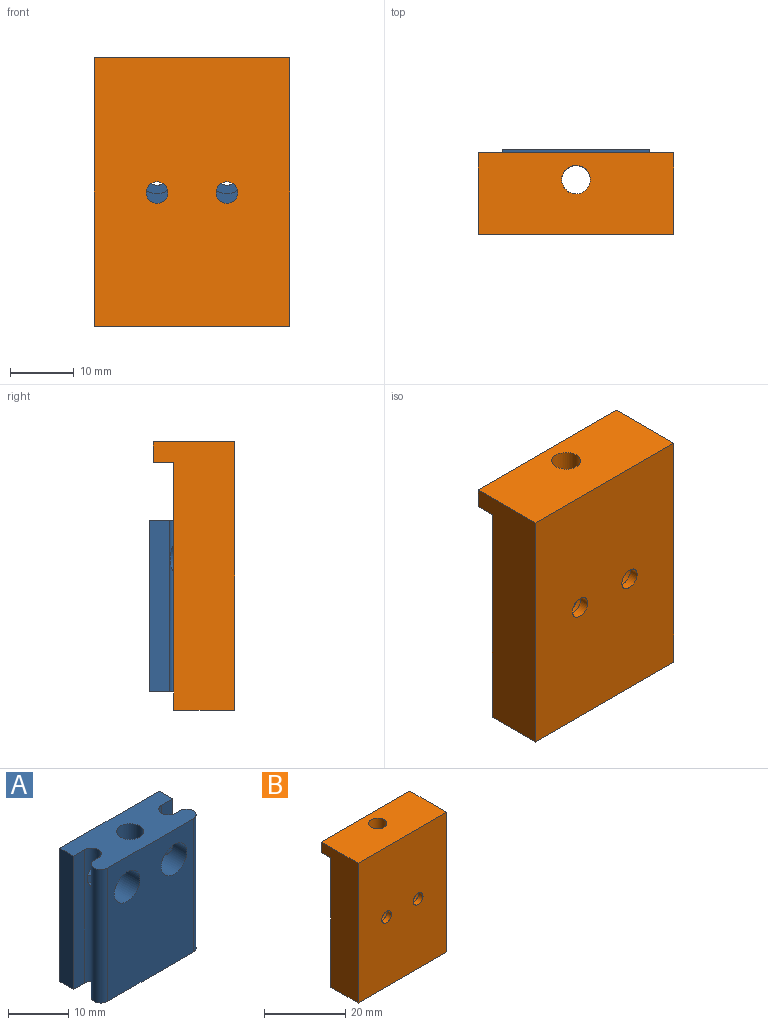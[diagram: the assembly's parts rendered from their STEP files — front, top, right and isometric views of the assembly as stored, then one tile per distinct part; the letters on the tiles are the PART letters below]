
ASSEMBLY  parts=2 mates=1
PART A: 28 faces, bbox 23.2x9.6x27 mm
  f0: plane 23.22x9.6mm, normal (0,0,-1), area 147.3mm2, adj f1,f2,f3,f4,f5,f6,f7,f8
  f1: cylinder r=1.6mm len=27mm, axis (0,0,-1), area 120.8mm2, adj f0,f3,f4,f13,f17
  f2: cylinder r=1.6mm len=27mm, axis (0,0,-1), area 120.8mm2, adj f0,f8,f9,f13,f16
  f3: plane 27x1mm, normal (0,1,0), area 27mm2, adj f0,f1,f12,f13
  f4: plane 27x2.6mm, normal (0,-1,0), area 70.2mm2, adj f0,f1,f5,f13
  f5: plane 27x3.2mm, normal (1,0,0), area 86.4mm2, adj f0,f4,f6,f13
  f6: plane 27x23.22mm, normal (0,1,0), area 608.8mm2, adj f0,f5,f7,f13,f14,f18
  f7: plane 27x3.2mm, normal (-1,0,0), area 86.4mm2, adj f0,f6,f8,f13
  f8: plane 27x2.6mm, normal (0,-1,0), area 70.2mm2, adj f0,f2,f7,f13
  f9: plane 27x1mm, normal (0,1,0), area 27mm2, adj f0,f2,f10,f13
  f10: cylinder r=1.6mm len=27mm, axis (0,0,-1), area 135.7mm2, adj f0,f9,f11,f13
  f11: plane 27x20mm, normal (0,-1,0), area 483.5mm2, adj f0,f10,f12,f13,f16,f17
  f12: cylinder r=1.6mm len=27mm, axis (0,0,-1), area 135.7mm2, adj f0,f3,f11,f13
  f13: plane 23.22x9.6mm, normal (0,0,1), area 180.1mm2, adj f1,f2,f3,f4,f5,f6,f7,f8
  f14: cylinder r=1.7mm len=3.4mm, axis (0,-1,0), area 16mm2, adj f6,f15
  f15: plane 6x6mm, normal (0,-1,0), area 19.2mm2, adj f14,f16
  f16: cylinder r=3mm len=8.1mm, axis (0,-1,0), area 139.4mm2, adj f2,f11,f15
  f17: cylinder r=3mm len=8.1mm, axis (0,-1,0), area 139.4mm2, adj f1,f11,f19
  f18: cylinder r=1.7mm len=3.4mm, axis (0,-1,0), area 16mm2, adj f6,f19
  f19: plane 6x6mm, normal (0,-1,0), area 19.2mm2, adj f17,f18
  f20: plane 4x3.75mm, normal (-0.87,0.5,0), area 17.3mm2, adj f0,f21,f25,f26
  f21: plane 4.33x4mm, normal (0,1,0), area 17.3mm2, adj f0,f20,f22,f26
  f22: plane 4x3.75mm, normal (0.87,0.5,0), area 17.3mm2, adj f0,f21,f23,f26
  f23: plane 4x3.75mm, normal (0.87,-0.5,0), area 17.3mm2, adj f0,f22,f24,f26
  f24: plane 4.33x4mm, normal (0,-1,0), area 17.3mm2, adj f0,f23,f25,f26
  f25: plane 4x3.75mm, normal (-0.87,-0.5,0), area 17.3mm2, adj f0,f20,f24,f26
  f26: plane 8.66x7.5mm, normal (0,0,-1), area 32.8mm2, adj f20,f21,f22,f23,f24,f25,f27
  f27: cylinder r=2.25mm len=23mm, axis (0,0,-1), area 325.2mm2, adj f13,f26
PART B: 23 faces, bbox 30.8x12.8x42.2 mm
  f0: plane 42.2x30.8mm, normal (0,-1,0), area 1281.6mm2, adj f1,f11,f12,f13,f16,f20
  f1: plane 42.2x12.8mm, normal (1,0,0), area 415.4mm2, adj f0,f2,f12,f19,f20,f21
  f2: plane 39x6.39mm, normal (0,1,0), area 249.2mm2, adj f1,f3,f12,f21
  f3: cylinder r=1mm len=39mm, axis (0,0,-1), area 122.2mm2, adj f2,f4,f12,f21
  f4: plane 39x1mm, normal (0,-1,0), area 38.9mm2, adj f3,f5,f12,f21
  f5: cylinder r=2.2mm len=39mm, axis (0,0,-1), area 269.5mm2, adj f4,f6,f12,f21
  f6: plane 39x20mm, normal (0,1,0), area 723.5mm2, adj f5,f7,f12,f15,f18,f21
  f7: cylinder r=2.2mm len=39mm, axis (0,0,-1), area 269.5mm2, adj f6,f8,f12,f21
  f8: plane 39x1mm, normal (0,-1,0), area 38.9mm2, adj f7,f9,f12,f21
  f9: cylinder r=1mm len=39mm, axis (0,0,-1), area 122.2mm2, adj f8,f10,f12,f21
  f10: plane 39x6.39mm, normal (0,1,0), area 249.2mm2, adj f9,f11,f12,f21
  f11: plane 42.2x12.8mm, normal (-1,0,0), area 415.4mm2, adj f0,f10,f12,f19,f20,f21
  f12: plane 30.8x9.6mm, normal (0,0,-1), area 159.6mm2, adj f0,f1,f2,f3,f4,f5,f6,f7
  f13: cylinder r=1.7mm len=3.4mm, axis (0,1,0), area 16mm2, adj f0,f14
  f14: plane 6x6mm, normal (0,1,0), area 19.2mm2, adj f13,f15
  f15: cylinder r=3mm len=6mm, axis (0,1,0), area 32mm2, adj f6,f14
  f16: cylinder r=1.7mm len=3.4mm, axis (0,1,0), area 16mm2, adj f0,f17
  f17: plane 6x6mm, normal (0,1,0), area 19.2mm2, adj f16,f18
  f18: cylinder r=3mm len=6mm, axis (0,1,0), area 32mm2, adj f6,f17
  f19: plane 30.8x3.2mm, normal (0,1,0), area 98.6mm2, adj f1,f11,f20,f21
  f20: plane 30.8x12.8mm, normal (0,0,1), area 378.3mm2, adj f0,f1,f11,f19,f22
  f21: plane 30.8x9.6mm, normal (0,0,-1), area 218.8mm2, adj f1,f2,f3,f4,f5,f6,f7,f8
  f22: cylinder r=2.25mm len=4.5mm, axis (0,0,-1), area 45.2mm2, adj f20,f21
PLACE A t=(-21.41,-10.52,-30.34)mm
PLACE B rot(axis=(0.3,-0.04,-0.95),0deg) t=(-21.41,-10.52,-27.19)mm
MATE slider A.f27 <-> B.f22  axis (0,0,-1) through (-21.41,-9.39,-16.84)mm
